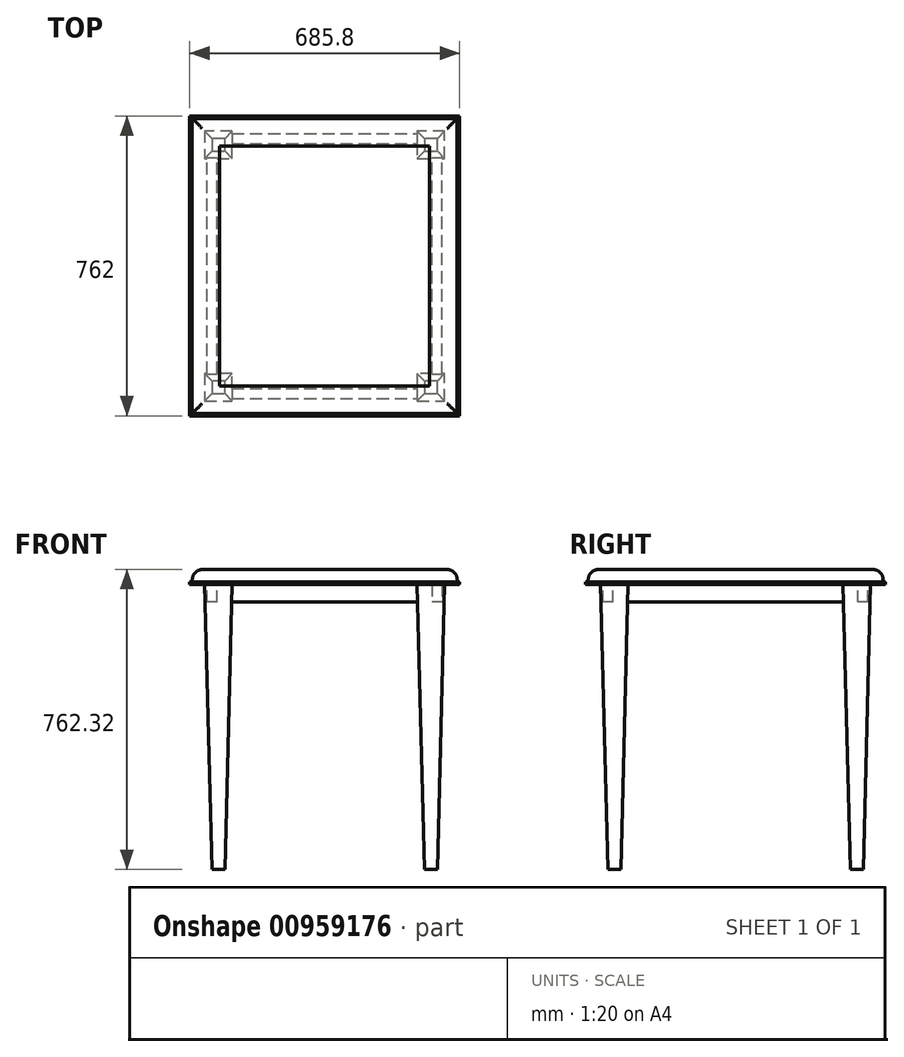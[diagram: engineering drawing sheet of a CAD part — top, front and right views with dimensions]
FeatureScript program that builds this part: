
annotation { "Feature Type Name" : "Feature", "Feature Type Description" : "" }
export const myFeature = defineFeature(function(context is Context, id is Id, definition is map)
    precondition{}
    {
        {
            var Q0;
            Q0=qCreatedBy(makeId("Top.planeOp"),FACE);
            var sketch = newSketch(context, id + "F0", { "sketchPlane" : qUnion([Q0])});
            skPoint(sketch, "E0.middle", {"position": v(0, 0) * mm});
            skLineSegment(sketch, "E1.0", {"start": v(-336.55, 374.65) * mm, "end": v(336.55, 374.65) * mm});
            skLineSegment(sketch, "E1.1", {"start": v(-336.55, 374.65) * mm, "end": v(-336.55, -374.65) * mm});
            skLineSegment(sketch, "E1.2", {"start": v(-336.55, -374.65) * mm, "end": v(336.55, -374.65) * mm});
            skLineSegment(sketch, "E1.3", {"start": v(336.55, 374.65) * mm, "end": v(336.55, -374.65) * mm});
            skSolve(sketch);
        }
        {
            var Q0;
            Q0=qCreatedBy(makeId("Top.planeOp"),FACE);
            var sketch = newSketch(context, id + "F1", { "sketchPlane" : qUnion([Q0])});
            skLineSegment(sketch, "E2.0", {"start": v(-342.9, 381) * mm, "end": v(-342.9, -381) * mm});
            skLineSegment(sketch, "E3.0", {"start": v(-342.9, 381) * mm, "end": v(342.9, 381) * mm});
            skLineSegment(sketch, "E4.0", {"start": v(342.9, 381) * mm, "end": v(342.9, -381) * mm});
            skLineSegment(sketch, "E5.0", {"start": v(-342.9, -381) * mm, "end": v(342.9, -381) * mm});
            skSolve(sketch);
        }
        {
            var Q0;
            Q0 = qSketchRegion(id + "F1", true);
            extrude(context, id + "F2", {"entities" : qUnion([Q0]), "depth" : 6.35 * mm, "offsetDistance" : 25.4 * mm});
        }
        {
            var Q0;
            Q0=qCreatedBy(makeId("Top.planeOp"),FACE);
            var sketch = newSketch(context, id + "F3", { "sketchPlane" : qUnion([Q0])});
            skLineSegment(sketch, "E6.0", {"start": v(-304.8, 342.9) * mm, "end": v(-234.95, 342.9) * mm});
            skLineSegment(sketch, "E6.1", {"start": v(-304.8, 342.9) * mm, "end": v(-304.8, 273.05) * mm});
            skLineSegment(sketch, "E6.2", {"start": v(-304.8, -342.9) * mm, "end": v(-234.95, -342.9) * mm});
            skLineSegment(sketch, "E6.3", {"start": v(304.8, 342.9) * mm, "end": v(304.8, 273.05) * mm});
            skLineSegment(sketch, "E7.top", {"start": v(-304.8, 273.05) * mm, "end": v(-234.95, 273.05) * mm});
            skLineSegment(sketch, "E7.right", {"start": v(-234.95, 342.9) * mm, "end": v(-234.95, 273.05) * mm});
            skLineSegment(sketch, "E8.1.0", {"start": v(234.95, -342.9) * mm, "end": v(234.95, -273.05) * mm});
            skLineSegment(sketch, "E8.1.1", {"start": v(304.8, -273.05) * mm, "end": v(234.95, -273.05) * mm});
            skPoint(sketch, "E8.center", {"position": v(0, 0) * mm});
            skLineSegment(sketch, "E9.bottom", {"start": v(304.8, 342.9) * mm, "end": v(234.95, 342.9) * mm});
            skLineSegment(sketch, "E9.top", {"start": v(304.8, 273.05) * mm, "end": v(234.95, 273.05) * mm});
            skLineSegment(sketch, "E9.right", {"start": v(234.95, 342.9) * mm, "end": v(234.95, 273.05) * mm});
            skLineSegment(sketch, "E10.1.0", {"start": v(-234.95, -342.9) * mm, "end": v(-234.95, -273.05) * mm});
            skLineSegment(sketch, "E10.1.1", {"start": v(-304.8, -273.05) * mm, "end": v(-234.95, -273.05) * mm});
            skLineSegment(sketch, "E11.trimOffspring", {"start": v(234.95, -342.9) * mm, "end": v(304.8, -342.9) * mm});
            skLineSegment(sketch, "E12.trimOffspring", {"start": v(-304.8, -273.05) * mm, "end": v(-304.8, -342.9) * mm});
            skLineSegment(sketch, "E13.trimOffspring", {"start": v(304.8, -273.05) * mm, "end": v(304.8, -342.9) * mm});
            skLineSegment(sketch, "E14.trimOffspring", {"start": v(234.95, 342.9) * mm, "end": v(304.8, 342.9) * mm});
            skSolve(sketch);
        }
        {
            var Q0;
            Q0 = qSketchRegion(id + "F3", true);
            extrude(context, id + "F4", {"entities" : qUnion([Q0]), "oppositeDirection" : true, "depth" : 723.9 * mm, "offsetDistance" : 25.4 * mm, "hasDraft" : true, "draftAngle" : 1.5 * degree, "draftPullDirection" : true});
        }
        {
            var Q0;
            Q0=qCreatedBy(makeId("Top.planeOp"),FACE);
            var sketch = newSketch(context, id + "F5", { "sketchPlane" : qUnion([Q0])});
            skLineSegment(sketch, "E15.bottom", {"start": v(-298.45, -336.55) * mm, "end": v(298.45, -336.55) * mm});
            skLineSegment(sketch, "E15.top", {"start": v(-298.45, 336.55) * mm, "end": v(298.45, 336.55) * mm});
            skLineSegment(sketch, "E15.left", {"start": v(-298.45, -336.55) * mm, "end": v(-298.45, 336.55) * mm});
            skLineSegment(sketch, "E15.right", {"start": v(298.45, -336.55) * mm, "end": v(298.45, 336.55) * mm});
            skPoint(sketch, "E15.middle", {"position": v(0, 0) * mm});
            skLineSegment(sketch, "E16.0", {"start": v(-273.05, -311.15) * mm, "end": v(273.05, -311.15) * mm});
            skLineSegment(sketch, "E16.1", {"start": v(-273.05, -311.15) * mm, "end": v(-273.05, 311.15) * mm});
            skLineSegment(sketch, "E16.2", {"start": v(-273.05, 311.15) * mm, "end": v(273.05, 311.15) * mm});
            skLineSegment(sketch, "E16.3", {"start": v(273.05, -311.15) * mm, "end": v(273.05, 311.15) * mm});
            skSolve(sketch);
        }
        {
            var Q0;
            Q0 = qSketchRegion(id + "F5", true);
            extrude(context, id + "F6", {"entities" : qUnion([Q0]), "oppositeDirection" : true, "depth" : 44.45 * mm, "offsetDistance" : 25.4 * mm});
        }
        {
            var Q0;
            Q0 = qSketchRegion(id + "F0", true);
            extrude(context, id + "F7", {"entities" : qUnion([Q0]), "operationType" : NewBodyOperationType.ADD, "depth" : 38.1 * mm, "offsetDistance" : 25.4 * mm});
        }
        {
            var Q0;
            Q0=makeQuery(id+"F7.opExtrude","CAP_EDGE",EDGE,{"disambiguationData":[OSD([sQuery(id+"F0.wireOp",EDGE,"E1.0")])],"isStart":false});
            var Q1;
            Q1=makeQuery(id+"F7.opExtrude","CAP_EDGE",EDGE,{"disambiguationData":[OSD([sQuery(id+"F0.wireOp",EDGE,"E1.3")])],"isStart":false});
            var Q2;
            Q2=makeQuery(id+"F7.opExtrude","CAP_EDGE",EDGE,{"disambiguationData":[OSD([sQuery(id+"F0.wireOp",EDGE,"E1.2")])],"isStart":false});
            var Q3;
            Q3=makeQuery(id+"F7.opExtrude","CAP_EDGE",EDGE,{"disambiguationData":[OSD([sQuery(id+"F0.wireOp",EDGE,"E1.1")])],"isStart":false});
            fillet(context, id + "F8", {"entities" : qUnion([Q0, Q1, Q2, Q3]), "radius" : 25.4 * mm, "tangentPropagation" : true, "allowEdgeOverflow" : false});
        }
        {
            var Q0;
            Q0=makeQuery(id+"F7.boolean.opBoolean","INTERSECT",EDGE,{"derivedFrom":[makeQuery(id+"F2.opExtrude","CAP_FACE",FACE,{"disambiguationData":[OSD([sQuery(id+"F1.wireOp",EDGE,"E2.0"),sQuery(id+"F1.wireOp",EDGE,"E3.0"),sQuery(id+"F1.wireOp",EDGE,"E4.0"),sQuery(id+"F1.wireOp",EDGE,"E5.0")])],"isStart":false}),makeQuery(id+"F7.opExtrude","SWEPT_FACE",FACE,{"disambiguationData":[OSD([sQuery(id+"F0.wireOp",EDGE,"E1.2")])]})]});
            var Q1;
            Q1=makeQuery(id+"F7.boolean.opBoolean","INTERSECT",EDGE,{"derivedFrom":[makeQuery(id+"F2.opExtrude","CAP_FACE",FACE,{"disambiguationData":[OSD([sQuery(id+"F1.wireOp",EDGE,"E2.0"),sQuery(id+"F1.wireOp",EDGE,"E3.0"),sQuery(id+"F1.wireOp",EDGE,"E4.0"),sQuery(id+"F1.wireOp",EDGE,"E5.0")])],"isStart":false}),makeQuery(id+"F7.opExtrude","SWEPT_FACE",FACE,{"disambiguationData":[OSD([sQuery(id+"F0.wireOp",EDGE,"E1.3")])]})]});
            var Q2;
            Q2=makeQuery(id+"F7.boolean.opBoolean","INTERSECT",EDGE,{"derivedFrom":[makeQuery(id+"F2.opExtrude","CAP_FACE",FACE,{"disambiguationData":[OSD([sQuery(id+"F1.wireOp",EDGE,"E2.0"),sQuery(id+"F1.wireOp",EDGE,"E3.0"),sQuery(id+"F1.wireOp",EDGE,"E4.0"),sQuery(id+"F1.wireOp",EDGE,"E5.0")])],"isStart":false}),makeQuery(id+"F7.opExtrude","SWEPT_FACE",FACE,{"disambiguationData":[OSD([sQuery(id+"F0.wireOp",EDGE,"E1.0")])]})]});
            var Q3;
            Q3=makeQuery(id+"F7.boolean.opBoolean","INTERSECT",EDGE,{"derivedFrom":[makeQuery(id+"F2.opExtrude","CAP_FACE",FACE,{"disambiguationData":[OSD([sQuery(id+"F1.wireOp",EDGE,"E2.0"),sQuery(id+"F1.wireOp",EDGE,"E3.0"),sQuery(id+"F1.wireOp",EDGE,"E4.0"),sQuery(id+"F1.wireOp",EDGE,"E5.0")])],"isStart":false}),makeQuery(id+"F7.opExtrude","SWEPT_FACE",FACE,{"disambiguationData":[OSD([sQuery(id+"F0.wireOp",EDGE,"E1.1")])]})]});
            fillet(context, id + "F9", {"entities" : qUnion([Q0, Q1, Q2, Q3]), "radius" : 6.35 * mm, "tangentPropagation" : true, "allowEdgeOverflow" : false});
        }
        {
            var Q0;
            Q0=makeQuery(id+"F7.opExtrude","CAP_FACE",FACE,{"disambiguationData":[OSD([sQuery(id+"F0.wireOp",EDGE,"E1.0"),sQuery(id+"F0.wireOp",EDGE,"E1.1"),sQuery(id+"F0.wireOp",EDGE,"E1.2"),sQuery(id+"F0.wireOp",EDGE,"E1.3")])],"isStart":false});
            var sketch = newSketch(context, id + "F10", { "sketchPlane" : qUnion([Q0])});
            skLineSegment(sketch, "E17.0", {"start": v(-266.7, 304.8) * mm, "end": v(266.7, 304.8) * mm});
            skLineSegment(sketch, "E17.1", {"start": v(-266.7, 304.8) * mm, "end": v(-266.7, -304.8) * mm});
            skLineSegment(sketch, "E17.2", {"start": v(-266.7, -304.8) * mm, "end": v(266.7, -304.8) * mm});
            skLineSegment(sketch, "E17.3", {"start": v(266.7, 304.8) * mm, "end": v(266.7, -304.8) * mm});
            skSolve(sketch);
        }
        {
            var Q0;
            Q0 = qSketchRegion(id + "F10", true);
            extrude(context, id + "F11", {"entities" : qUnion([Q0]), "depth" : 0.32 * mm, "offsetDistance" : 25.4 * mm});
        }
    });
